# Revit family: CENTUM Verbindungslasche XL100
name_source: partatom
category: HLS-Bauteile
revit_build: Autodesk Revit 2018 (Build: 20190510_1515(x64)
units: mm (PartAtom-declared; Revit-internal decimal feet)

## family parameters
Basisbauteil = Fläche
Beim Laden mit Abzugskörper schneiden = Nein
Bemaßung runder Anschluss = Durchmesser verwenden
Gemeinsam genutzt = Ja
Klassifizierung = Keine
Raumberechnungspunkt = Nein
Teiletyp = Normal

## types (1)
- Centum Verbindungslasche XL100
    Abmessung = 190x100
    Achsabstand Lochung = 100x60
    Artikelnummer = 1640003040
    Ausführung = paarweise verwenden
    Beschreibung = Montagehilfe, Fixierung oder Aufdopplung von CENTUM Profilen
    EAN = 4250928459718
    Fabrikat = MEFA
    Firma = MEFA Befestigungs- und Montagesysteme GmbH
    Gewicht = 1.29 kg
    Gewicht pro Bauteil = 1.29 kg
    Hersteller = MEFA
    Kurztext1 = Verbindungslasche
    Kurztext2 = für CENTUM XL 100
    Material = Stahl
    Mengeneinheit = St
    Oberflaeche = fsv.
    Vorgabe-Ansicht = 1219 mm
    vpe = 1
